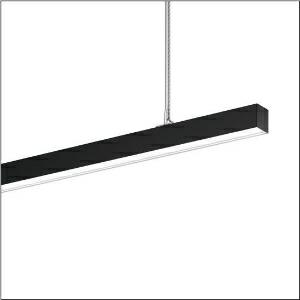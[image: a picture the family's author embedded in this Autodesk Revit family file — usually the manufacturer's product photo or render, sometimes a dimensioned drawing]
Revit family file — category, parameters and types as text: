
# Revit family: silica_21_51mx30da44bb
name_source: partatom
category: Lighting Fixtures
units: mm (PartAtom-declared; Revit-internal decimal feet)

## family parameters
Cut with Voids When Loaded = No
Host = Face
Light Source = No
Part Type = Normal
Room Calculation Point = No
Round Connector Dimension = Use Diameter
Shared = No

## types (1)
- --- (1 x LED, 4210 lm, 26 W, 4000K)
    Apparent Load = 26 VA
    CIE Flux Codes = 47 79 96 57 100
    Color Rendering = 80
    Color Temperature = 4000K
    Default Elevation = 1800 mm
    Description = Silica 21, office luminaire, primary optical cover: cover, of PMMA, opal, light emission: direct/indirect distribution, primary light characteristic: symmetric, installation type: suspended mounting, LED, rated luminous flux: 4.210lm, luminous efficacy: 162lm/W, light colour: 840, colour temperature: 4000K, control gear: DALI 2, with terminal, 3+2-pole, max. 2.5mm², mains connection: 220..240V, AC, 50/60Hz, rated input power: 26W, luminaire housing, of aluminium, matt jet black (RAL 9005), length: 1.204mm, width: 53mm, height: 53mm, protection rating (complete): IP20, insulation class (complete): insulation class I (protective earthing), certification: CE, permissible operating ambient temperature: 0..+35°C, standard: EN 50419, packaging unit: 1 piece
    Height = 53 mm
    Lamp = 1 x LED
    Lamp Light Flux = 4210 lm
    Lamp Power = 26 W
    Lamp count = 1
    Length = 1204 mm
    Luminous efficacy = 162 lm/W
    Manufacturer = Siteco
    ModVariant = No
    Model = 51MX30DA44BB
    Mounting Place = Ceiling
    Mounting Type = Pendant
    Number of Poles = 1
    OnlyDefault = Yes
    Power Factor = 1
    Product Name = Silica 21
    Product group = office luminaire | ceiling pendant
    ProductGroupID = 903
    Protection Class = Protection class I
    Protection Degree = IP 20
    RLX_Detail_Level = 1
    RLX_Emergency_Light_Flux = 0 lm
    RLX_Emergency_Type = 0
    RLX_Emergency_Type_DB = No
    RlxData = <blob elided: 25837 chars, md5=2c8c815f>
    Socket = socket
    Standby Power = 0 W
    System Light Flux = 4210 lm
    System Power = 26 W
    Type Comments = factory setting: luminous flux: 100 % | dim-lin: 254 | 218 mA
    Type Image = l_1335856.jpg
    URL = http://relux.com
    VarID = @adj_117517
    Voltage = 0 V
    Weight = 0.00 kg
    Width = 53 mm

## geometry (parser evidence)
native form markers: Blend x4, Sweep x15
no freeform markers — native parametric forms only
